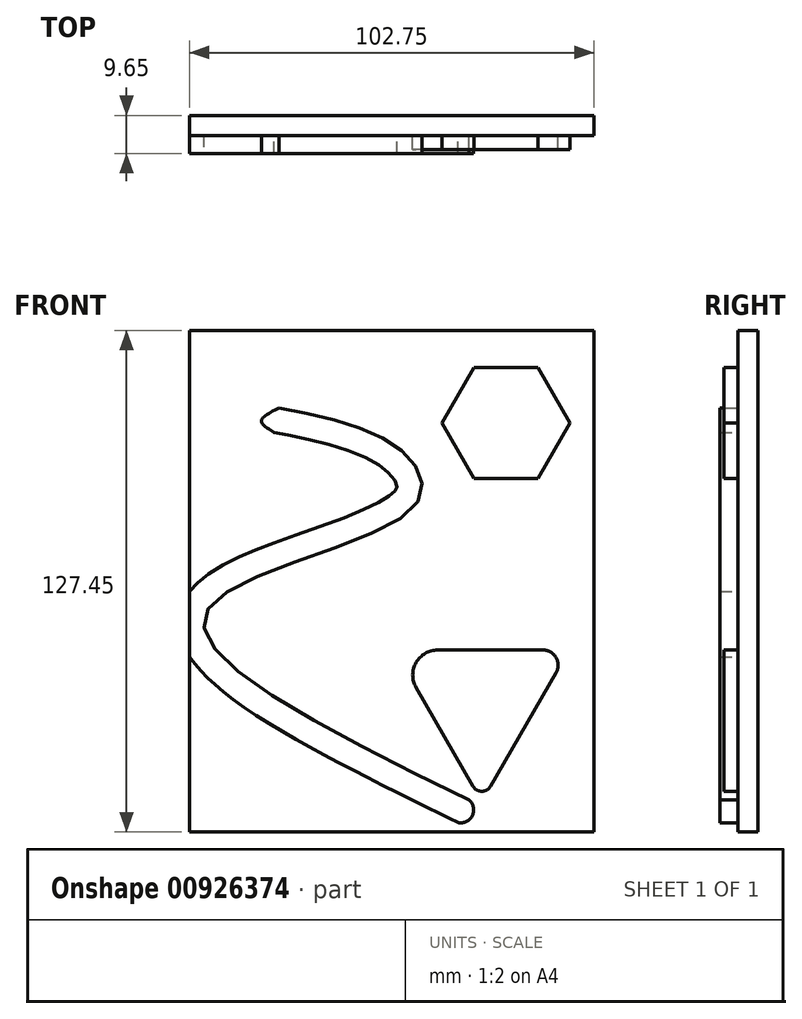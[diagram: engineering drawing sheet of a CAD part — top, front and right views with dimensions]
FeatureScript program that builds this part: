
annotation { "Feature Type Name" : "Feature", "Feature Type Description" : "" }
export const myFeature = defineFeature(function(context is Context, id is Id, definition is map)
    precondition{}
    {
        {
            var Q0;
            Q0=qCreatedBy(makeId("Front.planeOp"),FACE);
            var sketch = newSketch(context, id + "F0", { "sketchPlane" : qUnion([Q0])});
            skLineSegment(sketch, "E0.bottom", {"start": v(-63.73, 62.74) * mm, "end": v(39.02, 62.74) * mm});
            skLineSegment(sketch, "E0.top", {"start": v(-63.73, -64.7) * mm, "end": v(39.02, -64.7) * mm});
            skLineSegment(sketch, "E0.left", {"start": v(-63.73, 62.74) * mm, "end": v(-63.73, -64.7) * mm});
            skLineSegment(sketch, "E0.right", {"start": v(39.02, 62.74) * mm, "end": v(39.02, -64.7) * mm});
            skSolve(sketch);
        }
        {
            var Q0;
            Q0=makeQuery(id+"F0.imprint","IMPRINT",FACE,{"disambiguationData":[TD([[makeQuery(id+"F0.imprint","IMPRINT",EDGE,{"derivedFrom":sQuery(id+"F0.wireOp",EDGE,"E0.bottom")}),-1.0]])]});
            extrude(context, id + "F1", {"entities" : qUnion([Q0]), "depth" : 5.08 * mm, "offsetDistance" : 25.4 * mm});
        }
        {
            var Q0;
            Q0=makeQuery(id+"F1.opExtrude","CAP_FACE",FACE,{"disambiguationData":[OSD([sQuery(id+"F0.wireOp",EDGE,"E0.bottom"),sQuery(id+"F0.wireOp",EDGE,"E0.top"),sQuery(id+"F0.wireOp",EDGE,"E0.left"),sQuery(id+"F0.wireOp",EDGE,"E0.right")])],"isStart":false});
            var sketch = newSketch(context, id + "F2", { "sketchPlane" : qUnion([Q0])});
            skFitSpline(sketch, "E1", {"points": [v(-40.99, 43.1) * mm, v(-9.83, 32.14) * mm, v(-7.02, 17.55) * mm, v(-59.24, -8.28) * mm, v(7.3, -56.57) * mm], "startDerivative": vector(164.92, -33.49) * mm, "endDerivative": vector(320.54, -157.2) * mm});
            skFitSpline(sketch, "E2.0", {"points": [v(-42.25, 36.87) * mm, v(-40.53, 36.52) * mm, v(-37.13, 35.83) * mm, v(-32.2, 34.75) * mm, v(-27.56, 33.57) * mm, v(-23.3, 32.26) * mm, v(-19.51, 30.77) * mm, v(-16.86, 29.4) * mm, v(-15.07, 28.21) * mm, v(-13.9, 27.3) * mm, v(-12.88, 26.35) * mm, v(-12.07, 25.41) * mm, v(-11.49, 24.55) * mm, v(-11.14, 23.83) * mm, v(-11, 23.31) * mm, v(-10.98, 23.02) * mm, v(-11, 22.87) * mm, v(-11.06, 22.69) * mm, v(-11.2, 22.42) * mm, v(-11.37, 22.2) * mm, v(-11.55, 22) * mm, v(-11.76, 21.77) * mm, v(-12.14, 21.42) * mm, v(-12.75, 20.94) * mm, v(-13.76, 20.22) * mm, v(-15.38, 19.25) * mm, v(-17.79, 18.03) * mm, v(-21.5, 16.36) * mm, v(-26.88, 14.26) * mm, v(-34.01, 11.73) * mm, v(-40.11, 9.56) * mm, v(-44.88, 7.76) * mm, v(-48.34, 6.37) * mm, v(-51.66, 4.91) * mm, v(-54.8, 3.37) * mm, v(-57.72, 1.69) * mm, v(-59.96, 0.13) * mm, v(-61.62, -1.29) * mm, v(-62.8, -2.45) * mm, v(-63.7, -3.54) * mm, v(-64.37, -4.5) * mm, v(-64.99, -5.51) * mm, v(-65.64, -6.87) * mm, v(-66.19, -8.61) * mm, v(-66.47, -10.4) * mm, v(-66.5, -12.19) * mm, v(-66.29, -13.92) * mm, v(-65.74, -16.1) * mm, v(-64.65, -18.61) * mm, v(-62.9, -21.31) * mm, v(-60.8, -23.83) * mm, v(-58.38, -26.24) * mm, v(-54.75, -29.4) * mm, v(-49.49, -33.28) * mm, v(-42.13, -37.98) * mm, v(-33.88, -42.74) * mm, v(-24.9, -47.56) * mm, v(-15.4, -52.44) * mm, v(-5.52, -57.35) * mm, v(1.16, -60.63) * mm, v(4.5, -62.27) * mm]});
            skFitSpline(sketch, "E3", {"points": [v(-42.25, 36.87) * mm, v(-45.48, 39.72) * mm, v(-40.99, 43.1) * mm], "startDerivative": vector(-10.5, 6.06) * mm, "endDerivative": vector(12.52, 6.38) * mm});
            skArc(sketch, "E4", {"start": v(4.5, -62.27) * mm, "mid": v(8.13, -60.51) * mm, "end": v(7.3, -56.57) * mm});
            skSolve(sketch);
        }
        {
            var Q0;
            Q0=makeQuery(id+"F2.imprint","IMPRINT",FACE,{"disambiguationData":[TD([[makeQuery(id+"F2.imprint","IMPRINT",EDGE,{"derivedFrom":sQuery(id+"F2.wireOp",EDGE,"E1")}),-1.0]])]});
            extrude(context, id + "F3", {"entities" : qUnion([Q0]), "operationType" : NewBodyOperationType.ADD, "depth" : 4.57 * mm, "offsetDistance" : 25.4 * mm});
        }
        {
            var Q0;
            Q0=makeQuery(id+"F1.opExtrude","CAP_FACE",FACE,{"disambiguationData":[OSD([sQuery(id+"F0.wireOp",EDGE,"E0.bottom"),sQuery(id+"F0.wireOp",EDGE,"E0.top"),sQuery(id+"F0.wireOp",EDGE,"E0.left"),sQuery(id+"F0.wireOp",EDGE,"E0.right")])],"isStart":false});
            var sketch = newSketch(context, id + "F4", { "sketchPlane" : qUnion([Q0])});
            skCircle(sketch, "E5.cCircle", {"center": v(16.68, 39.21) * mm, "radius": 14.09 * mm, "construction": true});
            skLineSegment(sketch, "E5.0", {"start": v(24.82, 25.12) * mm, "end": v(8.55, 25.12) * mm});
            skLineSegment(sketch, "E5.1", {"start": v(8.55, 25.12) * mm, "end": v(0.42, 39.21) * mm});
            skLineSegment(sketch, "E5.2", {"start": v(0.42, 39.21) * mm, "end": v(8.55, 53.3) * mm});
            skLineSegment(sketch, "E5.3", {"start": v(8.55, 53.3) * mm, "end": v(24.82, 53.3) * mm});
            skLineSegment(sketch, "E5.4", {"start": v(24.82, 53.3) * mm, "end": v(32.95, 39.21) * mm});
            skLineSegment(sketch, "E5.5", {"start": v(32.95, 39.21) * mm, "end": v(24.82, 25.12) * mm});
            skPoint(sketch, "E5.0.midPoint", {"position": v(16.68, 25.12) * mm});
            skCircle(sketch, "E6.cCircle", {"center": v(10.52, -31.26) * mm, "radius": 12.81 * mm, "construction": true});
            skLineSegment(sketch, "E6.0", {"start": v(-0.68, -18.45) * mm, "end": v(26.05, -18.45) * mm});
            skLineSegment(sketch, "E6.1", {"start": v(29.38, -24.22) * mm, "end": v(12.72, -53.08) * mm});
            skLineSegment(sketch, "E6.2", {"start": v(8.32, -53.08) * mm, "end": v(-6.18, -27.97) * mm});
            skPoint(sketch, "E6.0.midPoint", {"position": v(10.52, -18.45) * mm});
            skPoint(sketch, "E7.visualSharp", {"position": v(-11.68, -18.45) * mm});
            skArc(sketch, "E7.filletArc", {"start": v(-0.68, -18.45) * mm, "mid": v(-6.18, -21.62) * mm, "end": v(-6.18, -27.97) * mm});
            skPoint(sketch, "E8.visualSharp", {"position": v(10.52, -56.9) * mm});
            skArc(sketch, "E8.filletArc", {"start": v(8.32, -53.08) * mm, "mid": v(10.52, -54.35) * mm, "end": v(12.72, -53.08) * mm});
            skPoint(sketch, "E9.visualSharp", {"position": v(32.71, -18.45) * mm});
            skArc(sketch, "E9.filletArc", {"start": v(29.38, -24.22) * mm, "mid": v(29.38, -20.37) * mm, "end": v(26.05, -18.45) * mm});
            skSolve(sketch);
        }
        {
            var Q0;
            Q0=makeQuery(id+"F4.imprint","IMPRINT",FACE,{"disambiguationData":[TD([[makeQuery(id+"F4.imprint","IMPRINT",EDGE,{"derivedFrom":sQuery(id+"F4.wireOp",EDGE,"E6.0")}),-1.0]])]});
            var Q1;
            Q1=makeQuery(id+"F4.imprint","IMPRINT",FACE,{"disambiguationData":[TD([[makeQuery(id+"F4.imprint","IMPRINT",EDGE,{"derivedFrom":sQuery(id+"F4.wireOp",EDGE,"E5.0")}),-1.0]])]});
            extrude(context, id + "F5", {"entities" : qUnion([Q0, Q1]), "operationType" : NewBodyOperationType.ADD, "depth" : 3.56 * mm, "offsetDistance" : 25.4 * mm});
        }
    });
